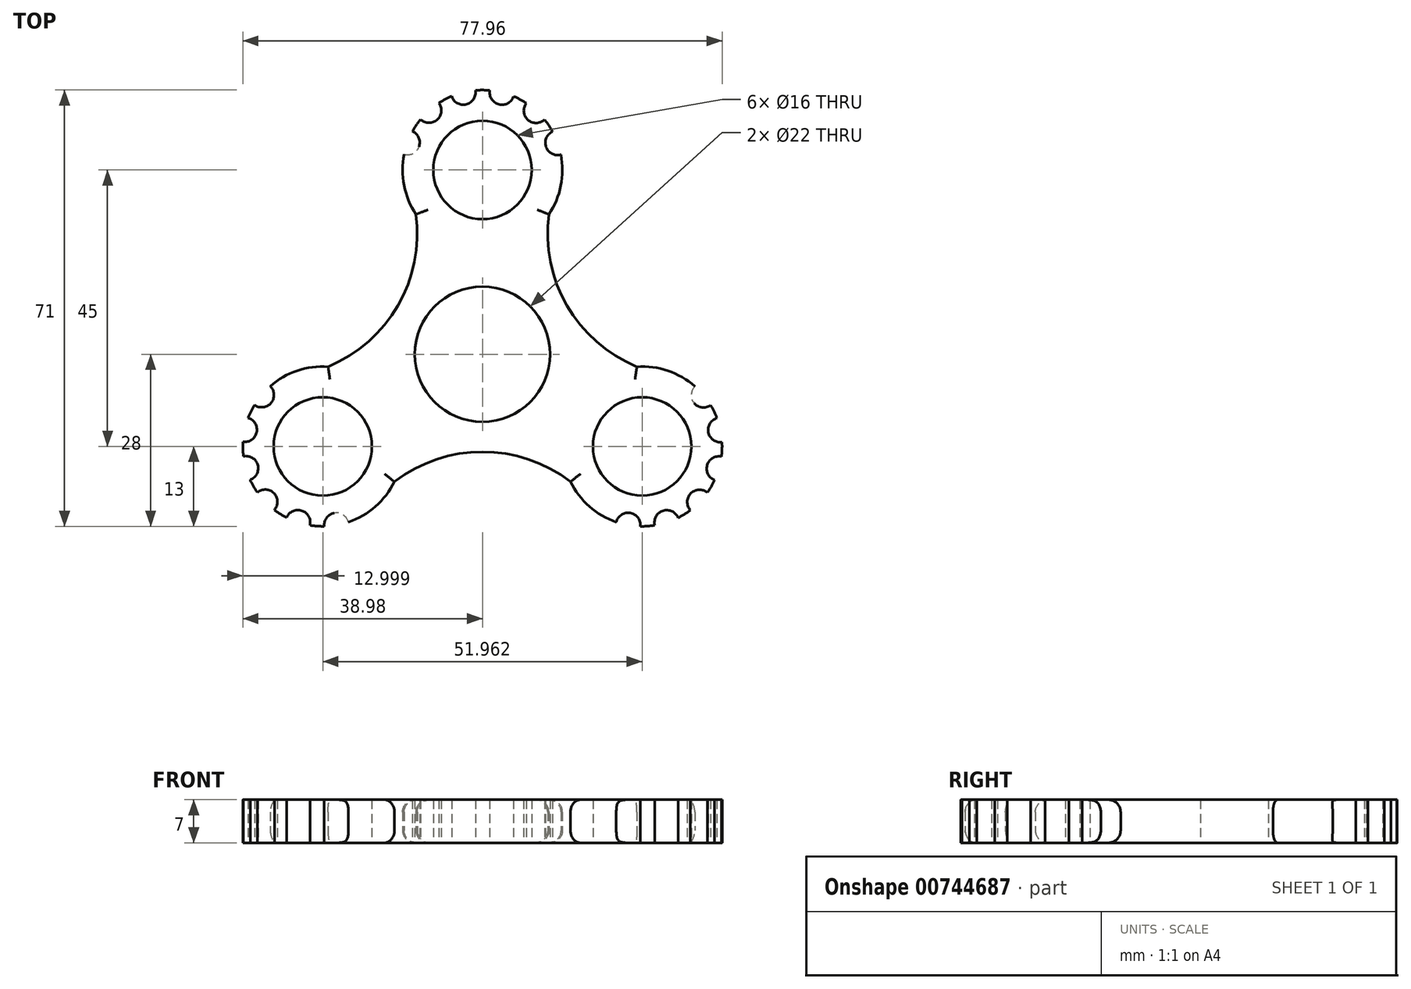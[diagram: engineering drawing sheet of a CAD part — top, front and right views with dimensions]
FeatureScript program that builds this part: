
annotation { "Feature Type Name" : "Feature", "Feature Type Description" : "" }
export const myFeature = defineFeature(function(context is Context, id is Id, definition is map)
    precondition{}
    {
        {
            var Q0;
            Q0=qCreatedBy(makeId("Top.planeOp"),FACE);
            var sketch = newSketch(context, id + "F0", { "sketchPlane" : qUnion([Q0])});
            skCircle(sketch, "E0", {"center": v(0, 0) * mm, "radius": 11 * mm});
            skCircle(sketch, "E1", {"center": v(0, 30) * mm, "radius": 8 * mm});
            skArc(sketch, "E2", {"start": v(1.2, 42.94) * mm, "mid": v(0.02, 43) * mm, "end": v(-1.15, 42.95) * mm});
            skArc(sketch, "E3", {"start": v(-12.75, 32.54) * mm, "mid": v(-10.33, 33.78) * mm, "end": v(-11.38, 36.29) * mm});
            skArc(sketch, "E4.1.0", {"start": v(-10.06, 38.23) * mm, "mid": v(-7.35, 38.19) * mm, "end": v(-7.1, 40.9) * mm});
            skArc(sketch, "E4.2.0", {"start": v(-5.02, 42) * mm, "mid": v(-2.64, 40.68) * mm, "end": v(-1.15, 42.95) * mm});
            skArc(sketch, "E4.3.0", {"start": v(1.2, 42.94) * mm, "mid": v(2.68, 40.67) * mm, "end": v(5.06, 41.97) * mm});
            skArc(sketch, "E4.4.0", {"start": v(7.13, 40.87) * mm, "mid": v(7.37, 38.16) * mm, "end": v(10.1, 38.2) * mm});
            skArc(sketch, "E4.5.0", {"start": v(11.4, 36.25) * mm, "mid": v(10.34, 33.74) * mm, "end": v(12.76, 32.5) * mm});
            skArc(sketch, "E5.trimOffspring", {"start": v(7.13, 40.87) * mm, "mid": v(6.12, 41.47) * mm, "end": v(5.06, 41.97) * mm});
            skArc(sketch, "E6.trimOffspring", {"start": v(11.4, 36.25) * mm, "mid": v(10.8, 37.25) * mm, "end": v(10.1, 38.2) * mm});
            skArc(sketch, "E7.trimOffspring", {"start": v(-5.02, 42) * mm, "mid": v(-6.08, 41.49) * mm, "end": v(-7.1, 40.9) * mm});
            skArc(sketch, "E8.trimOffspring", {"start": v(-10.06, 38.23) * mm, "mid": v(-10.76, 37.29) * mm, "end": v(-11.38, 36.29) * mm});
            skArc(sketch, "E9.trimOffspring", {"start": v(-12.75, 32.54) * mm, "mid": v(0, 17) * mm, "end": v(12.75, 32.54) * mm});
            skPoint(sketch, "E10.1.1", {"position": v(25.98, -15) * mm});
            skArc(sketch, "E10.1.2", {"start": v(38.88, -16.65) * mm, "mid": v(36.55, -18.05) * mm, "end": v(37.77, -20.48) * mm});
            skCircle(sketch, "E10.1.3", {"center": v(25.98, -15) * mm, "radius": 8 * mm});
            skArc(sketch, "E10.1.4", {"start": v(34.56, -5.23) * mm, "mid": v(34.42, -7.94) * mm, "end": v(37.11, -8.29) * mm});
            skArc(sketch, "E10.1.5", {"start": v(36.6, -22.5) * mm, "mid": v(33.88, -22.66) * mm, "end": v(33.82, -25.37) * mm});
            skArc(sketch, "E10.1.6", {"start": v(34.56, -5.23) * mm, "mid": v(14.72, -8.5) * mm, "end": v(21.8, -27.31) * mm});
            skLineSegment(sketch, "E10.1.7", {"start": v(25.98, -15) * mm, "end": v(25.7, -28) * mm, "construction": true});
            skLineSegment(sketch, "E10.1.8", {"start": v(25.98, -15) * mm, "end": v(34.56, -5.23) * mm, "construction": true});
            skArc(sketch, "E10.1.9", {"start": v(25.7, -28) * mm, "mid": v(24.05, -25.83) * mm, "end": v(21.76, -27.3) * mm});
            skArc(sketch, "E10.1.11", {"start": v(38.14, -10.4) * mm, "mid": v(36.74, -12.73) * mm, "end": v(38.96, -14.3) * mm});
            skArc(sketch, "E10.1.12", {"start": v(31.83, -26.61) * mm, "mid": v(29.36, -25.47) * mm, "end": v(28.03, -27.84) * mm});
            skArc(sketch, "E10.1.14", {"start": v(38.88, -16.65) * mm, "mid": v(38.97, -15.48) * mm, "end": v(38.96, -14.3) * mm});
            skArc(sketch, "E10.1.15", {"start": v(31.83, -26.61) * mm, "mid": v(32.85, -26.04) * mm, "end": v(33.82, -25.37) * mm});
            skArc(sketch, "E10.1.16", {"start": v(25.7, -28) * mm, "mid": v(26.86, -27.97) * mm, "end": v(28.03, -27.84) * mm});
            skArc(sketch, "E10.1.17", {"start": v(36.6, -22.5) * mm, "mid": v(37.23, -21.52) * mm, "end": v(37.77, -20.48) * mm});
            skArc(sketch, "E10.1.18", {"start": v(38.14, -10.4) * mm, "mid": v(37.68, -9.32) * mm, "end": v(37.11, -8.29) * mm});
            skPoint(sketch, "E10.2.1", {"position": v(-25.98, -15) * mm});
            skArc(sketch, "E10.2.2", {"start": v(-33.85, -25.34) * mm, "mid": v(-33.9, -22.63) * mm, "end": v(-36.62, -22.47) * mm});
            skCircle(sketch, "E10.2.3", {"center": v(-25.98, -15) * mm, "radius": 8 * mm});
            skArc(sketch, "E10.2.4", {"start": v(-21.8, -27.31) * mm, "mid": v(-24.09, -25.84) * mm, "end": v(-25.74, -28) * mm});
            skArc(sketch, "E10.2.5", {"start": v(-37.79, -20.44) * mm, "mid": v(-36.56, -18.01) * mm, "end": v(-38.88, -16.6) * mm});
            skArc(sketch, "E10.2.6", {"start": v(-21.8, -27.31) * mm, "mid": v(-14.72, -8.5) * mm, "end": v(-34.55, -5.23) * mm});
            skLineSegment(sketch, "E10.2.7", {"start": v(-25.98, -15) * mm, "end": v(-37.1, -8.25) * mm, "construction": true});
            skLineSegment(sketch, "E10.2.8", {"start": v(-25.98, -15) * mm, "end": v(-21.8, -27.31) * mm, "construction": true});
            skArc(sketch, "E10.2.9", {"start": v(-37.1, -8.25) * mm, "mid": v(-34.4, -7.91) * mm, "end": v(-34.52, -5.2) * mm});
            skArc(sketch, "E10.2.11", {"start": v(-28.08, -27.83) * mm, "mid": v(-29.4, -25.46) * mm, "end": v(-31.87, -26.6) * mm});
            skArc(sketch, "E10.2.12", {"start": v(-38.96, -14.26) * mm, "mid": v(-36.74, -12.7) * mm, "end": v(-38.12, -10.36) * mm});
            skArc(sketch, "E10.2.14", {"start": v(-33.85, -25.34) * mm, "mid": v(-32.89, -26.01) * mm, "end": v(-31.87, -26.6) * mm});
            skArc(sketch, "E10.2.15", {"start": v(-38.96, -14.26) * mm, "mid": v(-38.97, -15.43) * mm, "end": v(-38.88, -16.6) * mm});
            skArc(sketch, "E10.2.16", {"start": v(-37.1, -8.25) * mm, "mid": v(-37.66, -9.28) * mm, "end": v(-38.12, -10.36) * mm});
            skArc(sketch, "E10.2.17", {"start": v(-37.79, -20.44) * mm, "mid": v(-37.25, -21.48) * mm, "end": v(-36.62, -22.47) * mm});
            skArc(sketch, "E10.2.18", {"start": v(-28.08, -27.83) * mm, "mid": v(-26.91, -27.97) * mm, "end": v(-25.74, -28) * mm});
            skArc(sketch, "E11", {"start": v(14.32, -20.75) * mm, "mid": v(0, -15.87) * mm, "end": v(-14.32, -20.75) * mm});
            skArc(sketch, "E12", {"start": v(10.8, 22.77) * mm, "mid": v(13.74, 7.93) * mm, "end": v(25.13, -2.03) * mm});
            skArc(sketch, "E13", {"start": v(-25.13, -2.03) * mm, "mid": v(-13.74, 7.93) * mm, "end": v(-10.8, 22.77) * mm});
            skPoint(sketch, "E14.orphan", {"position": v(19.48, -26.26) * mm});
            skPoint(sketch, "E15.orphan", {"position": v(-19.48, -26.26) * mm});
            skPoint(sketch, "E16.orphan", {"position": v(-13, 30) * mm});
            skPoint(sketch, "E17.orphan", {"position": v(-32.48, -3.74) * mm});
            skSolve(sketch);
        }
        {
            var Q0;
            Q0=makeQuery(id+"F0.imprint","IMPRINT",FACE,{"disambiguationData":[TD([[makeQuery(id+"F0.imprint","IMPRINT",EDGE,{"derivedFrom":sQuery(id+"F0.wireOp",EDGE,"E10.1.2")}),-1.0]])]});
            var Q1;
            Q1=makeQuery(id+"F0.imprint","IMPRINT",FACE,{"disambiguationData":[TD([[makeQuery(id+"F0.imprint","IMPRINT",EDGE,{"derivedFrom":sQuery(id+"F0.wireOp",EDGE,"E10.2.3")}),1.0]])]});
            var Q2;
            Q2=makeQuery(id+"F0.imprint","IMPRINT",FACE,{"disambiguationData":[TD([[makeQuery(id+"F0.imprint","IMPRINT",EDGE,{"derivedFrom":sQuery(id+"F0.wireOp",EDGE,"E10.1.3")}),1.0]])]});
            var Q3;
            Q3=makeQuery(id+"F0.imprint","IMPRINT",FACE,{"disambiguationData":[TD([[makeQuery(id+"F0.imprint","IMPRINT",EDGE,{"derivedFrom":sQuery(id+"F0.wireOp",EDGE,"E0")}),-1.0]])]});
            var Q4;
            Q4=makeQuery(id+"F0.imprint","IMPRINT",FACE,{"disambiguationData":[TD([[makeQuery(id+"F0.imprint","IMPRINT",EDGE,{"derivedFrom":sQuery(id+"F0.wireOp",EDGE,"E0")}),1.0]])]});
            var Q5;
            Q5=makeQuery(id+"F0.imprint","IMPRINT",FACE,{"disambiguationData":[TD([[makeQuery(id+"F0.imprint","IMPRINT",EDGE,{"derivedFrom":sQuery(id+"F0.wireOp",EDGE,"E1")}),1.0]])]});
            var Q6;
            Q6=makeQuery(id+"F0.imprint","IMPRINT",FACE,{"disambiguationData":[TD([[makeQuery(id+"F0.imprint","IMPRINT",EDGE,{"derivedFrom":sQuery(id+"F0.wireOp",EDGE,"E1")}),-1.0]])]});
            var Q7;
            Q7=makeQuery(id+"F0.imprint","IMPRINT",FACE,{"disambiguationData":[TD([[makeQuery(id+"F0.imprint","IMPRINT",EDGE,{"derivedFrom":sQuery(id+"F0.wireOp",EDGE,"E10.2.2")}),-1.0]])]});
            extrude(context, id + "F1", {"entities" : qUnion([Q0, Q1, Q2, Q3, Q4, Q5, Q6, Q7]), "depth" : 7 * mm, "offsetDistance" : 25 * mm});
        }
        {
            var Q0;
            Q0=makeQuery(id+"F0.imprint","IMPRINT",FACE,{"disambiguationData":[TD([[makeQuery(id+"F0.imprint","IMPRINT",EDGE,{"derivedFrom":sQuery(id+"F0.wireOp",EDGE,"E10.2.3")}),1.0]])]});
            var Q1;
            Q1=makeQuery(id+"F0.imprint","IMPRINT",FACE,{"disambiguationData":[TD([[makeQuery(id+"F0.imprint","IMPRINT",EDGE,{"derivedFrom":sQuery(id+"F0.wireOp",EDGE,"E10.1.3")}),1.0]])]});
            var Q2;
            Q2=makeQuery(id+"F0.imprint","IMPRINT",FACE,{"disambiguationData":[TD([[makeQuery(id+"F0.imprint","IMPRINT",EDGE,{"derivedFrom":sQuery(id+"F0.wireOp",EDGE,"E1")}),1.0]])]});
            var Q3;
            Q3=makeQuery(id+"F0.imprint","IMPRINT",FACE,{"disambiguationData":[TD([[makeQuery(id+"F0.imprint","IMPRINT",EDGE,{"derivedFrom":sQuery(id+"F0.wireOp",EDGE,"E0")}),1.0]])]});
            extrude(context, id + "F2", {"entities" : qUnion([Q0, Q1, Q2, Q3]), "operationType" : NewBodyOperationType.REMOVE, "depth" : 7 * mm, "offsetDistance" : 25 * mm});
        }
        {
            var Q0;
            {var subQ0=sQuery(id+"F0.wireOp",EDGE,"E9.trimOffspring");Q0=makeQuery(id+"F1.opExtrude","CAP_EDGE",EDGE,{"disambiguationData":[OSD([subQ0]),TDD([makeQuery(id+"F0.imprint","IMPRINT",EDGE,{"disambiguationData":[TD([[makeQuery(id+"F0.imprint","INTERSECT",VERTEX,{"derivedFrom":[sQuery(id+"F0.wireOp",EDGE,"E3"),subQ0]}),-1.0]])],"derivedFrom":subQ0})])],"isStart":false});}
            var Q1;
            Q1=makeQuery(id+"F1.opExtrude","CAP_EDGE",EDGE,{"disambiguationData":[OSD([sQuery(id+"F0.wireOp",EDGE,"E13")])],"isStart":false});
            var Q2;
            {var subQ0=sQuery(id+"F0.wireOp",EDGE,"E10.2.6");Q2=makeQuery(id+"F1.opExtrude","CAP_EDGE",EDGE,{"disambiguationData":[OSD([subQ0]),TDD([makeQuery(id+"F0.imprint","IMPRINT",EDGE,{"disambiguationData":[TD([[makeQuery(id+"F0.imprint","INTERSECT",VERTEX,{"derivedFrom":[subQ0,sQuery(id+"F0.wireOp",EDGE,"E10.2.9")]}),1.0]])],"derivedFrom":subQ0})])],"isStart":false});}
            var Q3;
            {var subQ0=sQuery(id+"F0.wireOp",EDGE,"E10.2.6");Q3=makeQuery(id+"F1.opExtrude","CAP_EDGE",EDGE,{"disambiguationData":[OSD([subQ0]),TDD([makeQuery(id+"F0.imprint","IMPRINT",EDGE,{"disambiguationData":[TD([[makeQuery(id+"F0.imprint","INTERSECT",VERTEX,{"derivedFrom":[sQuery(id+"F0.wireOp",EDGE,"E10.2.4"),subQ0]}),-1.0]])],"derivedFrom":subQ0})])],"isStart":false});}
            var Q4;
            Q4=makeQuery(id+"F1.opExtrude","CAP_EDGE",EDGE,{"disambiguationData":[OSD([sQuery(id+"F0.wireOp",EDGE,"E11")])],"isStart":false});
            var Q5;
            {var subQ0=sQuery(id+"F0.wireOp",EDGE,"E10.1.6");Q5=makeQuery(id+"F1.opExtrude","CAP_EDGE",EDGE,{"disambiguationData":[OSD([subQ0]),TDD([makeQuery(id+"F0.imprint","IMPRINT",EDGE,{"disambiguationData":[TD([[makeQuery(id+"F0.imprint","INTERSECT",VERTEX,{"derivedFrom":[subQ0,sQuery(id+"F0.wireOp",EDGE,"E10.1.9")]}),1.0]])],"derivedFrom":subQ0})])],"isStart":false});}
            var Q6;
            {var subQ0=sQuery(id+"F0.wireOp",EDGE,"E10.1.6");Q6=makeQuery(id+"F1.opExtrude","CAP_EDGE",EDGE,{"disambiguationData":[OSD([subQ0]),TDD([makeQuery(id+"F0.imprint","IMPRINT",EDGE,{"disambiguationData":[TD([[makeQuery(id+"F0.imprint","INTERSECT",VERTEX,{"derivedFrom":[sQuery(id+"F0.wireOp",EDGE,"E10.1.4"),subQ0]}),-1.0]])],"derivedFrom":subQ0})])],"isStart":false});}
            var Q7;
            Q7=makeQuery(id+"F1.opExtrude","CAP_EDGE",EDGE,{"disambiguationData":[OSD([sQuery(id+"F0.wireOp",EDGE,"E12")])],"isStart":false});
            var Q8;
            {var subQ0=sQuery(id+"F0.wireOp",EDGE,"E9.trimOffspring");Q8=makeQuery(id+"F1.opExtrude","CAP_EDGE",EDGE,{"disambiguationData":[OSD([subQ0]),TDD([makeQuery(id+"F0.imprint","IMPRINT",EDGE,{"disambiguationData":[TD([[makeQuery(id+"F0.imprint","INTERSECT",VERTEX,{"derivedFrom":[sQuery(id+"F0.wireOp",EDGE,"E4.5.0"),subQ0]}),1.0]])],"derivedFrom":subQ0})])],"isStart":false});}
            var Q9;
            Q9=makeQuery(id+"F1.opExtrude","CAP_EDGE",EDGE,{"disambiguationData":[OSD([sQuery(id+"F0.wireOp",EDGE,"E13")])],"isStart":true});
            var Q10;
            {var subQ0=sQuery(id+"F0.wireOp",EDGE,"E10.2.6");Q10=makeQuery(id+"F1.opExtrude","CAP_EDGE",EDGE,{"disambiguationData":[OSD([subQ0]),TDD([makeQuery(id+"F0.imprint","IMPRINT",EDGE,{"disambiguationData":[TD([[makeQuery(id+"F0.imprint","INTERSECT",VERTEX,{"derivedFrom":[subQ0,sQuery(id+"F0.wireOp",EDGE,"E10.2.9")]}),1.0]])],"derivedFrom":subQ0})])],"isStart":true});}
            var Q11;
            {var subQ0=sQuery(id+"F0.wireOp",EDGE,"E9.trimOffspring");Q11=makeQuery(id+"F1.opExtrude","CAP_EDGE",EDGE,{"disambiguationData":[OSD([subQ0]),TDD([makeQuery(id+"F0.imprint","IMPRINT",EDGE,{"disambiguationData":[TD([[makeQuery(id+"F0.imprint","INTERSECT",VERTEX,{"derivedFrom":[sQuery(id+"F0.wireOp",EDGE,"E3"),subQ0]}),-1.0]])],"derivedFrom":subQ0})])],"isStart":true});}
            var Q12;
            {var subQ0=sQuery(id+"F0.wireOp",EDGE,"E10.2.6");Q12=makeQuery(id+"F1.opExtrude","CAP_EDGE",EDGE,{"disambiguationData":[OSD([subQ0]),TDD([makeQuery(id+"F0.imprint","IMPRINT",EDGE,{"disambiguationData":[TD([[makeQuery(id+"F0.imprint","INTERSECT",VERTEX,{"derivedFrom":[sQuery(id+"F0.wireOp",EDGE,"E10.2.4"),subQ0]}),-1.0]])],"derivedFrom":subQ0})])],"isStart":true});}
            var Q13;
            Q13=makeQuery(id+"F1.opExtrude","CAP_EDGE",EDGE,{"disambiguationData":[OSD([sQuery(id+"F0.wireOp",EDGE,"E11")])],"isStart":true});
            var Q14;
            {var subQ0=sQuery(id+"F0.wireOp",EDGE,"E10.1.6");Q14=makeQuery(id+"F1.opExtrude","CAP_EDGE",EDGE,{"disambiguationData":[OSD([subQ0]),TDD([makeQuery(id+"F0.imprint","IMPRINT",EDGE,{"disambiguationData":[TD([[makeQuery(id+"F0.imprint","INTERSECT",VERTEX,{"derivedFrom":[subQ0,sQuery(id+"F0.wireOp",EDGE,"E10.1.9")]}),1.0]])],"derivedFrom":subQ0})])],"isStart":true});}
            var Q15;
            {var subQ0=sQuery(id+"F0.wireOp",EDGE,"E10.1.6");Q15=makeQuery(id+"F1.opExtrude","CAP_EDGE",EDGE,{"disambiguationData":[OSD([subQ0]),TDD([makeQuery(id+"F0.imprint","IMPRINT",EDGE,{"disambiguationData":[TD([[makeQuery(id+"F0.imprint","INTERSECT",VERTEX,{"derivedFrom":[sQuery(id+"F0.wireOp",EDGE,"E10.1.4"),subQ0]}),-1.0]])],"derivedFrom":subQ0})])],"isStart":true});}
            var Q16;
            Q16=makeQuery(id+"F1.opExtrude","CAP_EDGE",EDGE,{"disambiguationData":[OSD([sQuery(id+"F0.wireOp",EDGE,"E12")])],"isStart":true});
            var Q17;
            {var subQ0=sQuery(id+"F0.wireOp",EDGE,"E9.trimOffspring");Q17=makeQuery(id+"F1.opExtrude","CAP_EDGE",EDGE,{"disambiguationData":[OSD([subQ0]),TDD([makeQuery(id+"F0.imprint","IMPRINT",EDGE,{"disambiguationData":[TD([[makeQuery(id+"F0.imprint","INTERSECT",VERTEX,{"derivedFrom":[sQuery(id+"F0.wireOp",EDGE,"E4.5.0"),subQ0]}),1.0]])],"derivedFrom":subQ0})])],"isStart":true});}
            fillet(context, id + "F3", {"entities" : qUnion([Q0, Q1, Q2, Q3, Q4, Q5, Q6, Q7, Q8, Q9, Q10, Q11, Q12, Q13, Q14, Q15, Q16, Q17]), "radius" : 2 * mm, "tangentPropagation" : true, "allowEdgeOverflow" : false});
        }
    });
